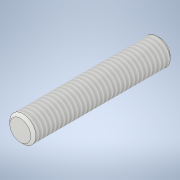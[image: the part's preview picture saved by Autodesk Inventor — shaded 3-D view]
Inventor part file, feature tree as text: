
AUTODESK INVENTOR PART (.ipt)
format: ipt  version: 2022 (Build 260153000, 153)  size: 114,688 bytes
history: native  units: in
note: dims shown in document units (in); Inventor stores cm internally (conversion verified against a paired STEP export)
features: extrude x1, chamfer x1, thread x1, sketch x1
ambient origin geometry x8: Origin, YZ Plane, XZ Plane, XY Plane, X Axis, Y Axis, Z Axis, Center Point
bodies: Body1 (feature_tree)
feature tree (4):
  extrude  "Extrusion1"  Depth=0.6299in
  chamfer  "Chamfer1"  Distance=0.0118in
  thread  "Thread1"  [1 undecoded]
  sketch  "Sketch1"  dims[d0=0.6299in d1=0.0in d2=0.0118in d3=0.0118in d4=17.7165in d5=0.0118in d6=0.0118in d7=17.7165in d8=0.6063in d9=0.0in]
note: 1 required parameter value undecoded (feature->parameter linkage not recoverable at this tier; creation-order binding heuristic only, values carry confidence <= 0.55)
